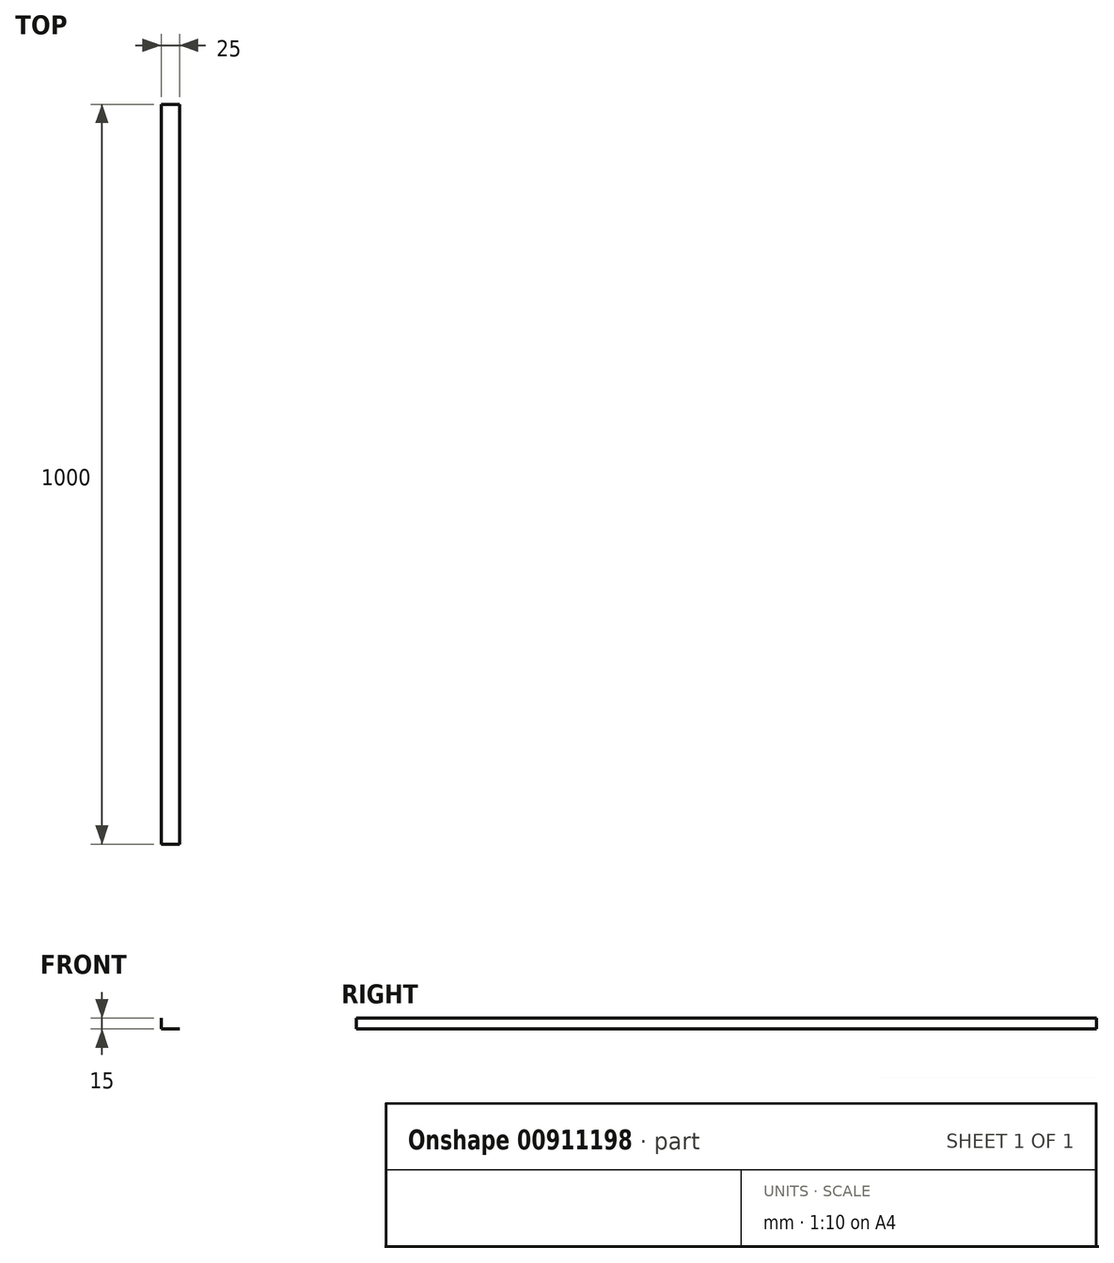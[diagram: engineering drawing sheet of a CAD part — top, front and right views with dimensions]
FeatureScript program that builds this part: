
annotation { "Feature Type Name" : "Feature", "Feature Type Description" : "" }
export const myFeature = defineFeature(function(context is Context, id is Id, definition is map)
    precondition{}
    {
        {
            var Q0;
            Q0=qCreatedBy(makeId("Front.planeOp"),FACE);
            var sketch = newSketch(context, id + "F0", { "sketchPlane" : qUnion([Q0])});
            skLineSegment(sketch, "E0", {"start": v(0, 15) * mm, "end": v(0, 0) * mm});
            skLineSegment(sketch, "E1", {"start": v(0, 0) * mm, "end": v(25, 0) * mm});
            skCircle(sketch, "E2", {"center": v(-52.4, 0) * mm, "radius": 11.45 * mm});
            skCircle(sketch, "E3", {"center": v(-52.4, 0) * mm, "radius": 17.2 * mm});
            skSolve(sketch);
        }
        {
            var Q0;
            Q0=sQuery(id+"F0.wireOp",EDGE,"E1");
            var Q1;
            Q1=sQuery(id+"F0.wireOp",EDGE,"E0");
            extrude(context, id + "F1", {"bodyType" : ToolBodyType.SURFACE, "surfaceEntities" : qUnion([Q0, Q1]), "depth" : 1000 * mm, "offsetDistance" : 25 * mm});
        }
    });
